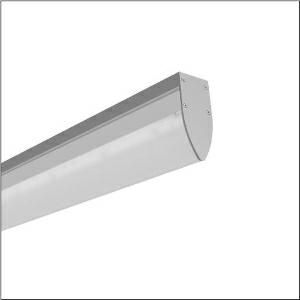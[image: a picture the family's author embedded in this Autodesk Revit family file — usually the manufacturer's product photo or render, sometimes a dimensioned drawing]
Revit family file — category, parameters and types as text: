
# Revit family: mira_r__21_td_51fr527g454a_bdf0
name_source: partatom
category: Lighting Fixtures
units: mm (PartAtom-declared; Revit-internal decimal feet)

## family parameters
Cut with Voids When Loaded = No
Host = Face
Light Source = No
Part Type = Normal
Room Calculation Point = No
Round Connector Dimension = Use Diameter
Shared = No

## types (1)
- Mira® 21 TD (1 x LED, 5500 lm, 39 W, 4000K)
    Apparent Load = 39 VA
    CIE Flux Codes = 40 68 87 81 100
    Color Rendering = 80
    Color Temperature = 4000K
    Default Elevation = 1800 mm
    Description = Mira® 21 TD, clean room luminaire, primary light control with reflector, primary optical cover: cover, of PMMA, frosted, light emission: direct distribution, primary light characteristic: symmetric, installation type: surface-mounted, LED, rated luminous flux: 5.500lm, luminous efficacy: 141lm/W, light colour: 840, colour temperature: 4000K, control gear: ON/OFF, with terminal, 3-pole, max. 2.5mm², mains connection: 230V, AC, 50/60Hz, rated input power: 39W, luminaire housing, of sheet steel, coated, pure white (RAL 9010), length: 900mm, width: 55mm, height: 120mm, protection rating (complete): IP43, insulation class (complete): insulation class I (protective earthing), certification: CE, UKCA, permissible operating ambient temperature: -5..+40°C, standard: EN 50419, packaging unit: 1 piece
    Height = 120 mm
    Lamp = 1 x LED
    Lamp Light Flux = 5500 lm
    Lamp Power = 39 W
    Lamp count = 1
    Length = 900 mm
    Luminous efficacy = 141 lm/W
    Manufacturer = Siteco
    ModVariant = No
    Model = 51FR527G454A
    Mounting Place = Ceiling
    Mounting Type = Surface mounted
    Number of Poles = 1
    OnlyDefault = Yes
    Power Factor = 1
    Product Name = Mira® 21 TD
    Product group = clean room luminaire | ceiling mounted
    ProductGroupID = 306
    Protection Class = Protection class I
    Protection Degree = IP 43
    RLX_Detail_Level = 1
    RLX_Emergency_Light_Flux = 0 lm
    RLX_Emergency_Type = 0
    RLX_Emergency_Type_DB = No
    RlxData = <blob elided: 25145 chars, md5=f771d664>
    Socket = socket
    Standby Power = 0 W
    System Light Flux = 5500 lm
    System Power = 39 W
    Type Comments = Product without accessories
    Type Image = l_1007115.jpg
    URL = http://relux.com
    VarID = ---
    Voltage = 0 V
    Weight = 0.00 kg
    Width = 55 mm

## geometry (parser evidence)
native form markers: Blend x4, Sweep x14
no freeform markers — native parametric forms only
